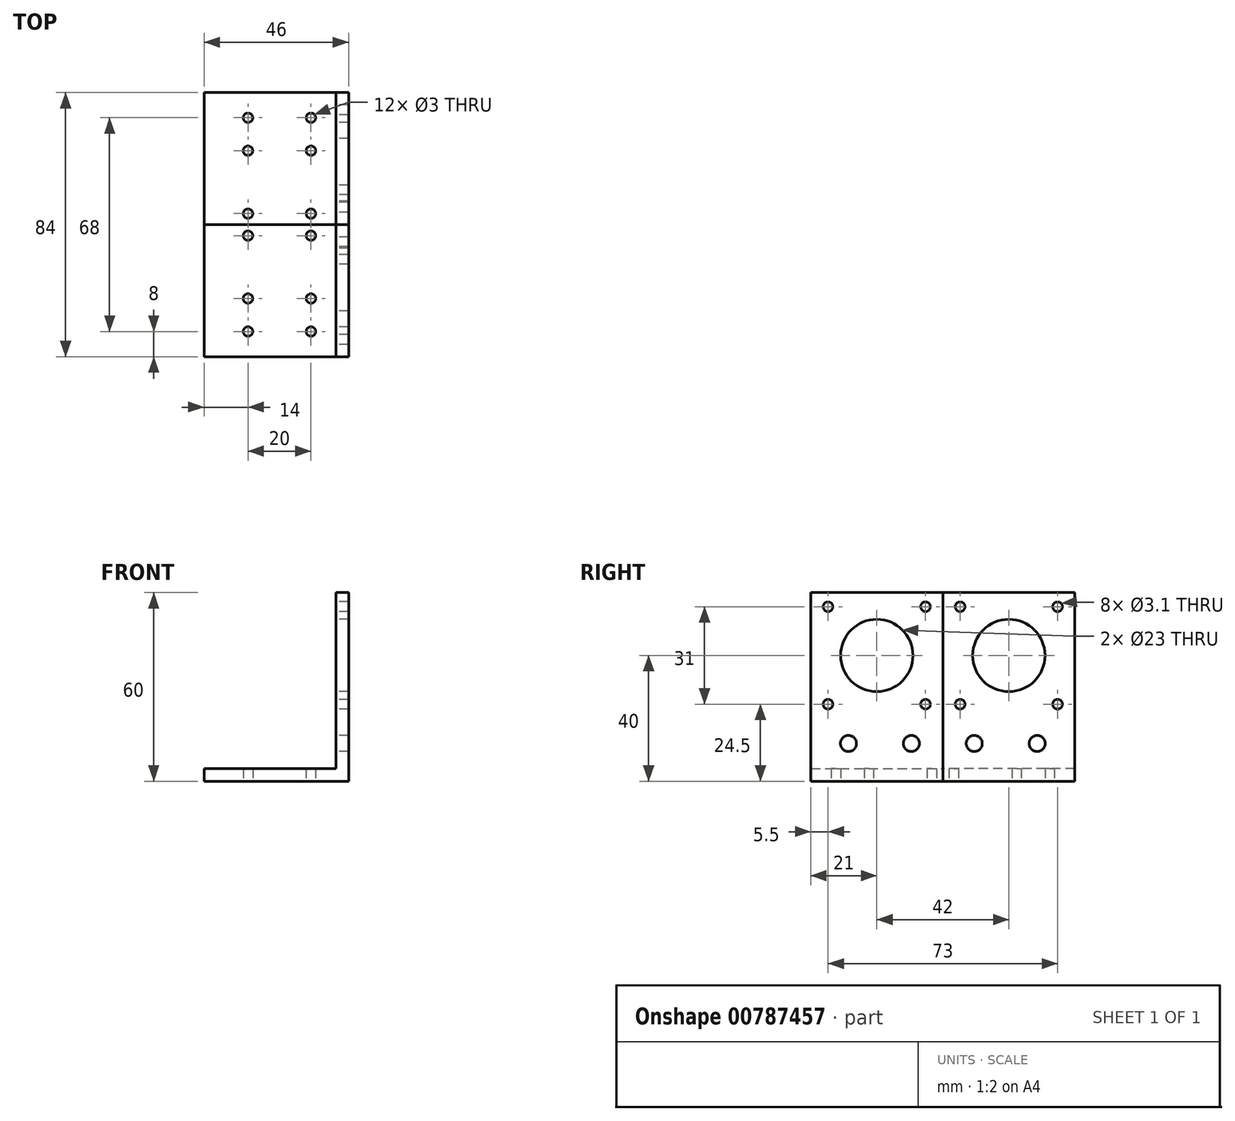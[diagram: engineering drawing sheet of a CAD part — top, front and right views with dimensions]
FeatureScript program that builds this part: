
annotation { "Feature Type Name" : "Feature", "Feature Type Description" : "" }
export const myFeature = defineFeature(function(context is Context, id is Id, definition is map)
    precondition{}
    {
        {
            var Q0;
            Q0=qCreatedBy(makeId("Front.planeOp"),FACE);
            var sketch = newSketch(context, id + "F0", { "sketchPlane" : qUnion([Q0])});
            skLineSegment(sketch, "E0.bottom", {"start": v(0, 0) * mm, "end": v(46, 0) * mm});
            skLineSegment(sketch, "E0.right", {"start": v(46, 0) * mm, "end": v(46, 25) * mm});
            skLineSegment(sketch, "E1.top", {"start": v(0, 4) * mm, "end": v(42, 4) * mm});
            skLineSegment(sketch, "E1.right", {"start": v(42, 23) * mm, "end": v(42, 4) * mm});
            skLineSegment(sketch, "E2", {"start": v(46, 25) * mm, "end": v(46, 60) * mm});
            skLineSegment(sketch, "E3", {"start": v(46, 60) * mm, "end": v(42, 60) * mm});
            skLineSegment(sketch, "E4", {"start": v(42, 60) * mm, "end": v(42, 23) * mm});
            skLineSegment(sketch, "E5", {"start": v(0, 0) * mm, "end": v(0, 4) * mm});
            skSolve(sketch);
        }
        {
            var Q0;
            Q0=makeQuery(id+"F0.imprint","IMPRINT",FACE,{"disambiguationData":[TD([[makeQuery(id+"F0.imprint","IMPRINT",EDGE,{"derivedFrom":sQuery(id+"F0.wireOp",EDGE,"E0.bottom")}),1.0]])]});
            extrude(context, id + "F1", {"entities" : qUnion([Q0]), "depth" : 42 * mm, "offsetDistance" : 25 * mm});
        }
        {
            var Q0;
            Q0=makeQuery(id+"F1.opExtrude","SWEPT_FACE",FACE,{"disambiguationData":[OSD([sQuery(id+"F0.wireOp",EDGE,"E0.bottom")])]});
            var sketch = newSketch(context, id + "F2", { "sketchPlane" : qUnion([Q0])});
            skLineSegment(sketch, "E6", {"start": v(24, 0) * mm, "end": v(24, 42) * mm, "construction": true});
            skLineSegment(sketch, "E7", {"start": v(0, 13.5) * mm, "end": v(46, 13.5) * mm, "construction": true});
            skLineSegment(sketch, "E8", {"start": v(46, 13.5) * mm, "end": v(45.2, 14.22) * mm, "construction": true});
            skCircle(sketch, "E9", {"center": v(14, 3.5) * mm, "radius": 1.5 * mm});
            skCircle(sketch, "E10.MirrorC", {"center": v(34, 3.5) * mm, "radius": 1.5 * mm});
            skCircle(sketch, "E11.MirrorC", {"center": v(14, 23.5) * mm, "radius": 1.5 * mm});
            skCircle(sketch, "E12.MirrorC", {"center": v(34, 23.5) * mm, "radius": 1.5 * mm});
            skLineSegment(sketch, "E13", {"start": v(46, 34) * mm, "end": v(0, 34) * mm, "construction": true});
            skCircle(sketch, "E14", {"center": v(34, 34) * mm, "radius": 1.5 * mm});
            skCircle(sketch, "E15.MirrorC", {"center": v(14, 34) * mm, "radius": 1.5 * mm});
            skSolve(sketch);
        }
        {
            var Q0;
            Q0 = qSketchRegion(id + "F2", true);
            extrude(context, id + "F3", {"entities" : qUnion([Q0]), "operationType" : NewBodyOperationType.REMOVE, "oppositeDirection" : true, "depth" : 25 * mm, "offsetDistance" : 25 * mm});
        }
        {
            var Q0;
            Q0=makeQuery(id+"F1.opExtrude","SWEPT_FACE",FACE,{"disambiguationData":[OSD([sQuery(id+"F0.wireOp",EDGE,"E1.right")])]});
            var sketch = newSketch(context, id + "F4", { "sketchPlane" : qUnion([Q0])});
            skLineSegment(sketch, "E16", {"start": v(0, 12) * mm, "end": v(42, 12) * mm, "construction": true});
            skPoint(sketch, "E16.endSnap0", {"position": v(0, 32) * mm});
            skCircle(sketch, "E17", {"center": v(10, 12) * mm, "radius": 2.55 * mm});
            skCircle(sketch, "E18", {"center": v(30, 12) * mm, "radius": 2.55 * mm});
            skSolve(sketch);
        }
        {
            var Q0;
            Q0 = qSketchRegion(id + "F4", true);
            extrude(context, id + "F5", {"entities" : qUnion([Q0]), "operationType" : NewBodyOperationType.REMOVE, "endBound" : BoundingType.UP_TO_NEXT, "oppositeDirection" : true, "depth" : 25 * mm, "offsetDistance" : 25 * mm});
        }
        {
            var Q0;
            Q0=makeQuery(id+"F1.opExtrude","SWEPT_FACE",FACE,{"disambiguationData":[OSD([sQuery(id+"F0.wireOp",EDGE,"E1.right"),sQuery(id+"F0.wireOp",EDGE,"E4")])]});
            var sketch = newSketch(context, id + "F6", { "sketchPlane" : qUnion([Q0])});
            skLineSegment(sketch, "E19", {"start": v(21, 60) * mm, "end": v(21, 10) * mm, "construction": true});
            skLineSegment(sketch, "E20", {"start": v(1, 40) * mm, "end": v(41, 40) * mm, "construction": true});
            skCircle(sketch, "E21", {"center": v(5.5, 55.5) * mm, "radius": 1.55 * mm});
            skCircle(sketch, "E22.MirrorC", {"center": v(36.5, 55.5) * mm, "radius": 1.55 * mm});
            skCircle(sketch, "E23.MirrorC", {"center": v(5.5, 24.5) * mm, "radius": 1.55 * mm});
            skCircle(sketch, "E24.MirrorC", {"center": v(36.5, 24.5) * mm, "radius": 1.55 * mm});
            skCircle(sketch, "E25", {"center": v(21, 40) * mm, "radius": 11.5 * mm});
            skSolve(sketch);
        }
        {
            var Q0;
            Q0 = qSketchRegion(id + "F6", true);
            extrude(context, id + "F7", {"entities" : qUnion([Q0]), "operationType" : NewBodyOperationType.REMOVE, "endBound" : BoundingType.UP_TO_NEXT, "oppositeDirection" : true, "depth" : 25 * mm, "offsetDistance" : 25 * mm});
        }
        {
            var Q0;
            Q0=makeQuery(id+"F1.opExtrude","SWEPT_BODY",BODY,{"disambiguationData":[OSD([sQuery(id+"F0.wireOp",EDGE,"E0.bottom"),sQuery(id+"F0.wireOp",EDGE,"E0.right"),sQuery(id+"F0.wireOp",EDGE,"E1.top"),sQuery(id+"F0.wireOp",EDGE,"E1.right"),sQuery(id+"F0.wireOp",EDGE,"E2"),sQuery(id+"F0.wireOp",EDGE,"E3"),sQuery(id+"F0.wireOp",EDGE,"E4"),sQuery(id+"F0.wireOp",EDGE,"E5")])]});
            var Q1;
            Q1=qCreatedBy(makeId("Front.planeOp"),FACE);
            mirror(context, id + "F8", {"entities" : qUnion([Q0]), "mirrorPlane" : qUnion([Q1])});
        }
    });
